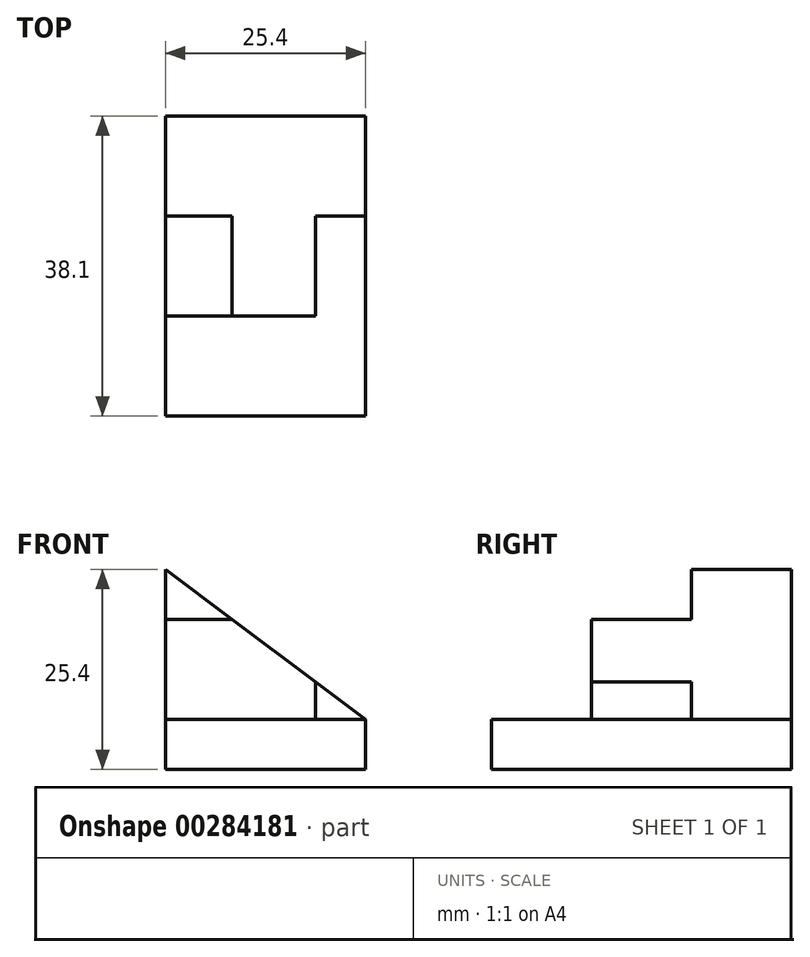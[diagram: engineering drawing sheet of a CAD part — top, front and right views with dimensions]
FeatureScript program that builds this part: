
annotation { "Feature Type Name" : "Feature", "Feature Type Description" : "" }
export const myFeature = defineFeature(function(context is Context, id is Id, definition is map)
    precondition{}
    {
        {
            var Q0;
            Q0=qCreatedBy(makeId("Front.planeOp"),FACE);
            var sketch = newSketch(context, id + "F0", { "sketchPlane" : qUnion([Q0])});
            skLineSegment(sketch, "E0", {"start": v(0, 0) * mm, "end": v(25.4, 0) * mm});
            skLineSegment(sketch, "E1", {"start": v(25.4, 0) * mm, "end": v(25.4, 6.35) * mm});
            skLineSegment(sketch, "E2", {"start": v(25.4, 6.35) * mm, "end": v(0, 25.4) * mm});
            skLineSegment(sketch, "E3", {"start": v(0, 25.4) * mm, "end": v(0, 6.35) * mm});
            skLineSegment(sketch, "E4", {"start": v(0, 6.35) * mm, "end": v(0, 0) * mm});
            skLineSegment(sketch, "E5", {"start": v(0, 6.35) * mm, "end": v(25.4, 6.35) * mm});
            skLineSegment(sketch, "E6", {"start": v(0, 20.64) * mm, "end": v(6.35, 20.64) * mm});
            skLineSegment(sketch, "E7", {"start": v(16.93, 6.35) * mm, "end": v(16.93, 12.7) * mm});
            skSolve(sketch);
        }
        {
            var Q0;
            Q0 = qSketchRegion(id + "F0", true);
            extrude(context, id + "F1", {"entities" : qUnion([Q0]), "depth" : 38.1 * mm, "symmetric" : true});
        }
        {
            var Q0;
            Q0=makeQuery(id+"F1.opExtrude","SWEPT_FACE",FACE,{"disambiguationData":[OSD([sQuery(id+"F0.wireOp",EDGE,"E3"),sQuery(id+"F0.wireOp",EDGE,"E4")])]});
            var sketch = newSketch(context, id + "F2", { "sketchPlane" : qUnion([Q0])});
            skLineSegment(sketch, "E8", {"start": v(19.05, 6.35) * mm, "end": v(6.35, 6.35) * mm});
            skLineSegment(sketch, "E9", {"start": v(6.35, 6.35) * mm, "end": v(6.35, 19.05) * mm});
            skLineSegment(sketch, "E10", {"start": v(6.35, 19.05) * mm, "end": v(-6.35, 19.05) * mm});
            skLineSegment(sketch, "E11", {"start": v(-6.35, 19.05) * mm, "end": v(-6.35, 25.4) * mm});
            skLineSegment(sketch, "E12", {"start": v(-6.35, 25.4) * mm, "end": v(19.05, 25.4) * mm});
            skLineSegment(sketch, "E13", {"start": v(19.05, 25.4) * mm, "end": v(19.05, 6.35) * mm});
            skSolve(sketch);
        }
        {
            var Q0;
            Q0 = qSketchRegion(id + "F2", true);
            extrude(context, id + "F3", {"entities" : qUnion([Q0]), "operationType" : NewBodyOperationType.REMOVE, "endBound" : BoundingType.THROUGH_ALL, "oppositeDirection" : true, "depth" : 25.4 * mm});
        }
        {
            var Q0;
            Q0=makeQuery(id+"F3.boolean.opBoolean","COPY",FACE,{"derivedFrom":makeQuery(id+"F3.opExtrude","SWEPT_FACE",FACE,{"disambiguationData":[OSD([sQuery(id+"F2.wireOp",EDGE,"E9")])]})});
            var sketch = newSketch(context, id + "F4", { "sketchPlane" : qUnion([Q0])});
            skLineSegment(sketch, "E14", {"start": v(25.4, 6.35) * mm, "end": v(19.05, 6.35) * mm});
            skLineSegment(sketch, "E15", {"start": v(19.05, 6.35) * mm, "end": v(19.05, 11.11) * mm});
            skLineSegment(sketch, "E16", {"start": v(19.05, 11.11) * mm, "end": v(25.4, 6.35) * mm});
            skSolve(sketch);
        }
        {
            var Q0;
            Q0 = qSketchRegion(id + "F4", true);
            extrude(context, id + "F5", {"entities" : qUnion([Q0]), "operationType" : NewBodyOperationType.REMOVE, "oppositeDirection" : true, "depth" : 12.7 * mm});
        }
    });
